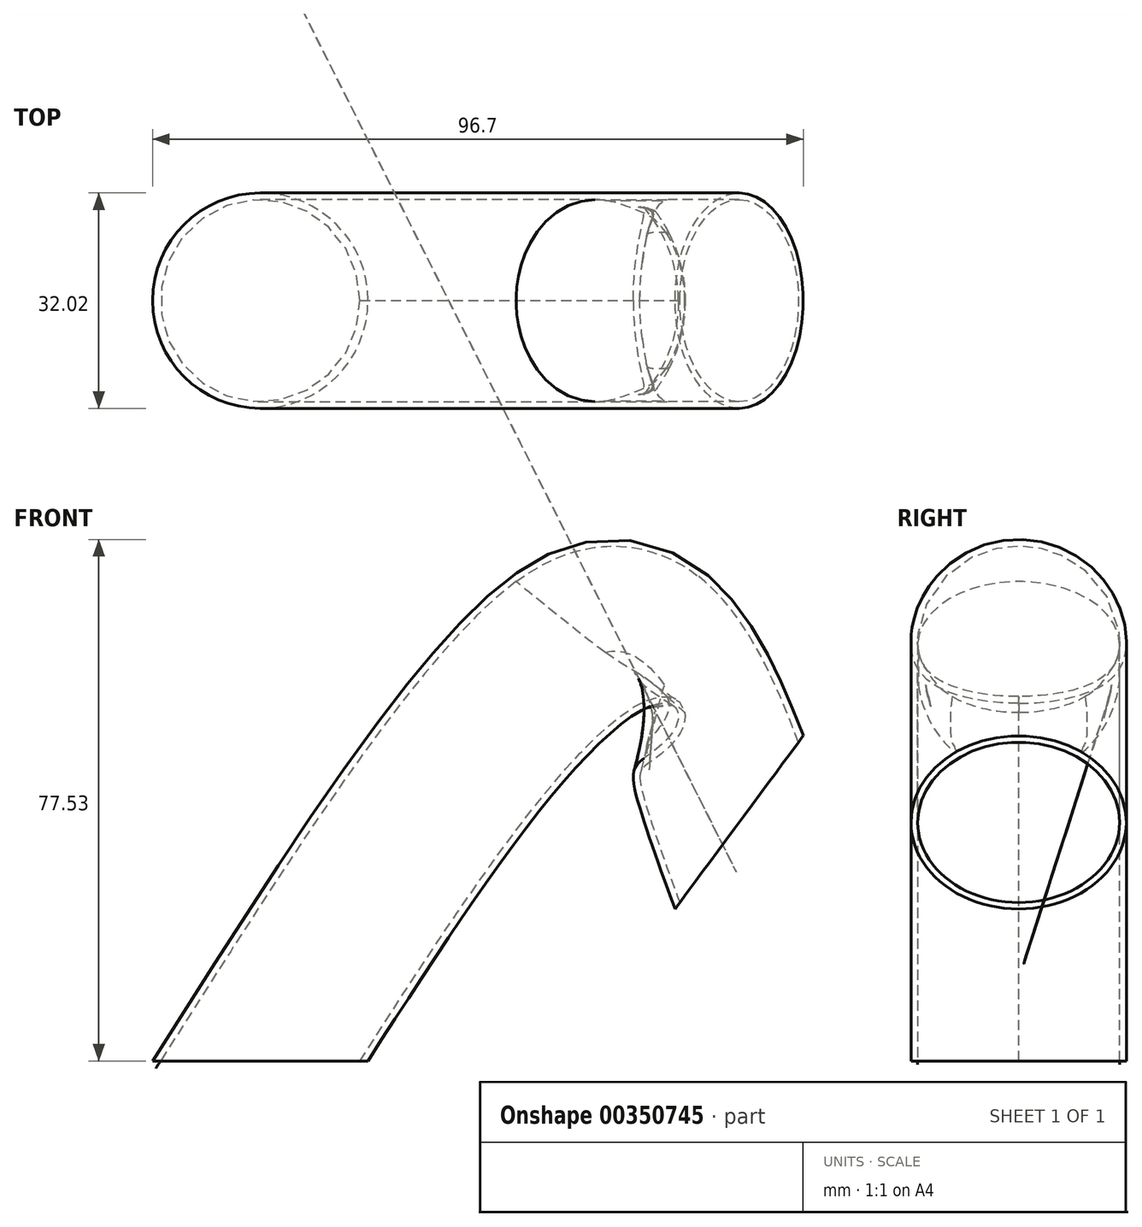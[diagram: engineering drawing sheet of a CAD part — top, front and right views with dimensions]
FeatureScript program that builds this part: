
annotation { "Feature Type Name" : "Feature", "Feature Type Description" : "" }
export const myFeature = defineFeature(function(context is Context, id is Id, definition is map)
    precondition{}
    {
        {
            var Q0;
            Q0=qCreatedBy(makeId("Top.planeOp"),FACE);
            var sketch = newSketch(context, id + "F0", { "sketchPlane" : qUnion([Q0])});
            skCircle(sketch, "E0", {"center": v(0, 0) * mm, "radius": 19.9 * mm});
            skCircle(sketch, "E1", {"center": v(0, 0) * mm, "radius": 16 * mm});
            skSolve(sketch);
        }
        {
            var Q0;
            Q0=qCreatedBy(makeId("Front.planeOp"),FACE);
            var sketch = newSketch(context, id + "F1", { "sketchPlane" : qUnion([Q0])});
            skFitSpline(sketch, "E2", {"points": [v(0, 0) * mm, v(53.1, 62.35) * mm, v(71.17, 35.47) * mm], "startDerivative": vector(98.68, 154.11) * mm, "endDerivative": vector(39.13, -102.67) * mm});
            skSolve(sketch);
        }
        {
            var Q0;
            Q0=makeQuery(id+"F0.imprint","IMPRINT",FACE,{"disambiguationData":[TD([[makeQuery(id+"F0.imprint","IMPRINT",EDGE,{"derivedFrom":sQuery(id+"F0.wireOp",EDGE,"E1")}),1.0]])]});
            var Q1;
            Q1=sQuery(id+"F1.wireOp",EDGE,"E2");
            sweep(context, id + "F2", {"profiles" : qUnion([Q0]), "path" : qUnion([Q1])});
        }
        {
            var Q0;
            Q0=makeQuery(id+"F2.opSweep","CAP_FACE",FACE,{"disambiguationData":[OSD([sQuery(id+"F0.wireOp",EDGE,"E1"),sQuery(id+"F1.wireOp",VERTEX,"E2.start")])],"isStart":true});
            var Q1;
            Q1=makeQuery(id+"F2.opSweep","CAP_FACE",FACE,{"disambiguationData":[OSD([sQuery(id+"F0.wireOp",EDGE,"E1"),sQuery(id+"F1.wireOp",VERTEX,"E2.end")])],"isStart":false});
            shell(context, id + "F3", {"entities" : qUnion([Q0, Q1]), "thickness" : 1 * mm});
        }
    });
